# Revit family: Building-IEC309Connections-GEWISS-COMBIBLOC-INTERLOCKED-SOCKET-OUTLETS_IP44_WITHOUT_BOTTOM
name_source: partatom
category: Apparecchi elettrici
units: mm (PartAtom-declared; Revit-internal decimal feet)

## family parameters
Condiviso = No
Host = Superficie
Mantenere orientamento annotazione = Sì
Punto di calcolo locali = Sì
Quota connettore circolare = Usa diametro
Taglio con vuoti quando caricato = No
Tipo di parte = Normale

## types (18) — shared parameters
BLOCCO = B=C
Catalogue = BUILDING
Electrocod = 2220
FORMULA = 1000 mm  [stored 3.28084 ft]
Frequency = 50/60 Hz
Glow wire test: = 850 °C (active parts) - 650 °C (passive parts)
IDF = dd829b8d-9985-4c4e-bf32-3d5e44e427e2
IDT = 741e4717e3ee4884b61990f959ff1807
IP degree = IP44
Immagine tipo = COMBIBLOC44.jpg
L = 155 mm
N.poli = 1
Operating temperature: = -25 +40 °C
POMELLO = bianco
PRESA = Giallo
Produttore = GEWISS S.p.A.
Prospetto di default = 1219 mm
Protection = NO (SBF)
SEO = Interlocked outlet
STRUTTURA = RAL - 7035
STRUTTURA ALTA = blue
Shock resistance = IK08
Spostamento_S = 1500 mm
Technical sheet = https://www.gewiss.com
Thermo-pressure with ball = 125
Typology = Compact
URL = https://www.gewiss.com
VETRO = Vetro
Version file RFA = 21.4
Voltaggio = 0 V
W = 115 mm
With back-mounting box = No

## per-type parameters (varying)
| type | Colour: | Descrizione | Modello | No. of poles | Rated current (A) | Rated voltage | Reference h |
| GW66431 - COMBIBLOC N.B.IP44 3P+N+E 16A 400V 6H | Red | COMBIBLOC N.B.IP44 3P+N+E 16A 400V 6H | GW66431 | 3P+N+E | 16 | 380-415V | 6 |
| GW66423 - COMBIBLOC N.B.IP44 2P+E 16A 110V 4H | Yellow | COMBIBLOC N.B.IP44 2P+E 16A 110V 4H | GW66423 | 2P+E | 16 | 100-130V | 4 |
| GW66429 - COMBIBLOC N.B.IP44 2P+E 16A 400V 9H | Red | COMBIBLOC N.B.IP44 2P+E 16A 400V 9H | GW66429 | 2P+E | 16 | 380-415V | 9 |
| GW66436 - COMBIBLOC N.B.IP44 3P+N+E 32A 110V 4H | Yellow | COMBIBLOC N.B.IP44 3P+N+E 32A 110V 4H | GW66436 | 3P+N+E | 32 | 100-130V | 4 |
| GW66435 - COMBIBLOC N.B.IP44 3P+E 32A 110V 4H | Yellow | COMBIBLOC N.B.IP44 3P+E 32A 110V 4H | GW66435 | 3P+E | 32 | 100-130V | 4 |
| GW66434 - COMBIBLOC N.B.IP44 2P+E 32A 110V 4H | Yellow | COMBIBLOC N.B.IP44 2P+E 32A 110V 4H | GW66434 | 2P+E | 32 | 100-130V | 4 |
| GW66427 - COMBIBLOC N.B.IP44 3P+E 16A 230V 9H | Blue | COMBIBLOC N.B.IP44 3P+E 16A 230V 9H | GW66427 | 3P+E | 16 | 200-250V | 9 |
| GW66425 - COMBIBLOC N.B.IP44 3P+N+E 16A 110V 4H | Yellow | COMBIBLOC N.B.IP44 3P+N+E 16A 110V 4H | GW66425 | 3P+N+E | 16 | 100-130V | 4 |
| GW66430 - COMBIBLOC N.B.IP44 3P+E 16A 400V 6H | Red | COMBIBLOC N.B.IP44 3P+E 16A 400V 6H | GW66430 | 3P+E | 16 | 380-415V | 6 |
| GW66424 - COMBIBLOC N.B.IP44 3P+E 16A 110V 4H | Yellow | COMBIBLOC N.B.IP44 3P+E 16A 110V 4H | GW66424 | 3P+E | 16 | 100-130V | 4 |
| GW66428 - COMBIBLOC N.B.IP44 3P+N+E 16A 230V 9H | Blue | COMBIBLOC N.B.IP44 3P+N+E 16A 230V 9H | GW66428 | 3P+N+E | 16 | 200-250V | 9 |
| GW66437 - COMBIBLOC N.B.IP44 2P+E 32A 230V 6H | Blue | COMBIBLOC N.B.IP44 2P+E 32A 230V 6H | GW66437 | 2P+E | 32 | 200-250V | 6 |
| GW66426 - COMBIBLOC N.B.IP44 2P+E 16A 230V 6H | Blue | COMBIBLOC N.B.IP44 2P+E 16A 230V 6H | GW66426 | 2P+E | 16 | 200-250V | 6 |
| GW66441 - COMBIBLOC N.B.IP44 3P+E 32A 400V 6H | Red | COMBIBLOC N.B.IP44 3P+E 32A 400V 6H | GW66441 | 3P+E | 32 | 380-415V | 6 |
| GW66438 - COMBIBLOC N.B.IP44 3P+E 32A 230V 9H | Blue | COMBIBLOC N.B.IP44 3P+E 32A 230V 9H | GW66438 | 3P+E | 32 | 200-250V | 9 |
| GW66440 - COMBIBLOC N.B.IP44 2P+E 32A 400V 9H | Red | COMBIBLOC N.B.IP44 2P+E 32A 400V 9H | GW66440 | 2P+E | 32 | 380-415V | 9 |
| GW66439 - COMBIBLOC N.B.IP44 3P+N+E 32A 230V 9H | Blue | COMBIBLOC N.B.IP44 3P+N+E 32A 230V 9H | GW66439 | 3P+N+E | 32 | 200-250V | 9 |
| GW66442 - COMBIBLOC N.B.IP44 3P+N+E 32A 400V 6H | Red | COMBIBLOC N.B.IP44 3P+N+E 32A 400V 6H | GW66442 | 3P+N+E | 32 | 380-415V | 6 |

note: source unit labels omitted for Thermo-pressure with ball — the stored unit's dimension contradicts the parameter name (converter mislabeling)

note: [stored X ft] marks values corroborated as IEEE doubles in the binary element streams (Revit-internal decimal feet)

## geometry (parser evidence)
native form markers: Sweep x4
no freeform markers — native parametric forms only
